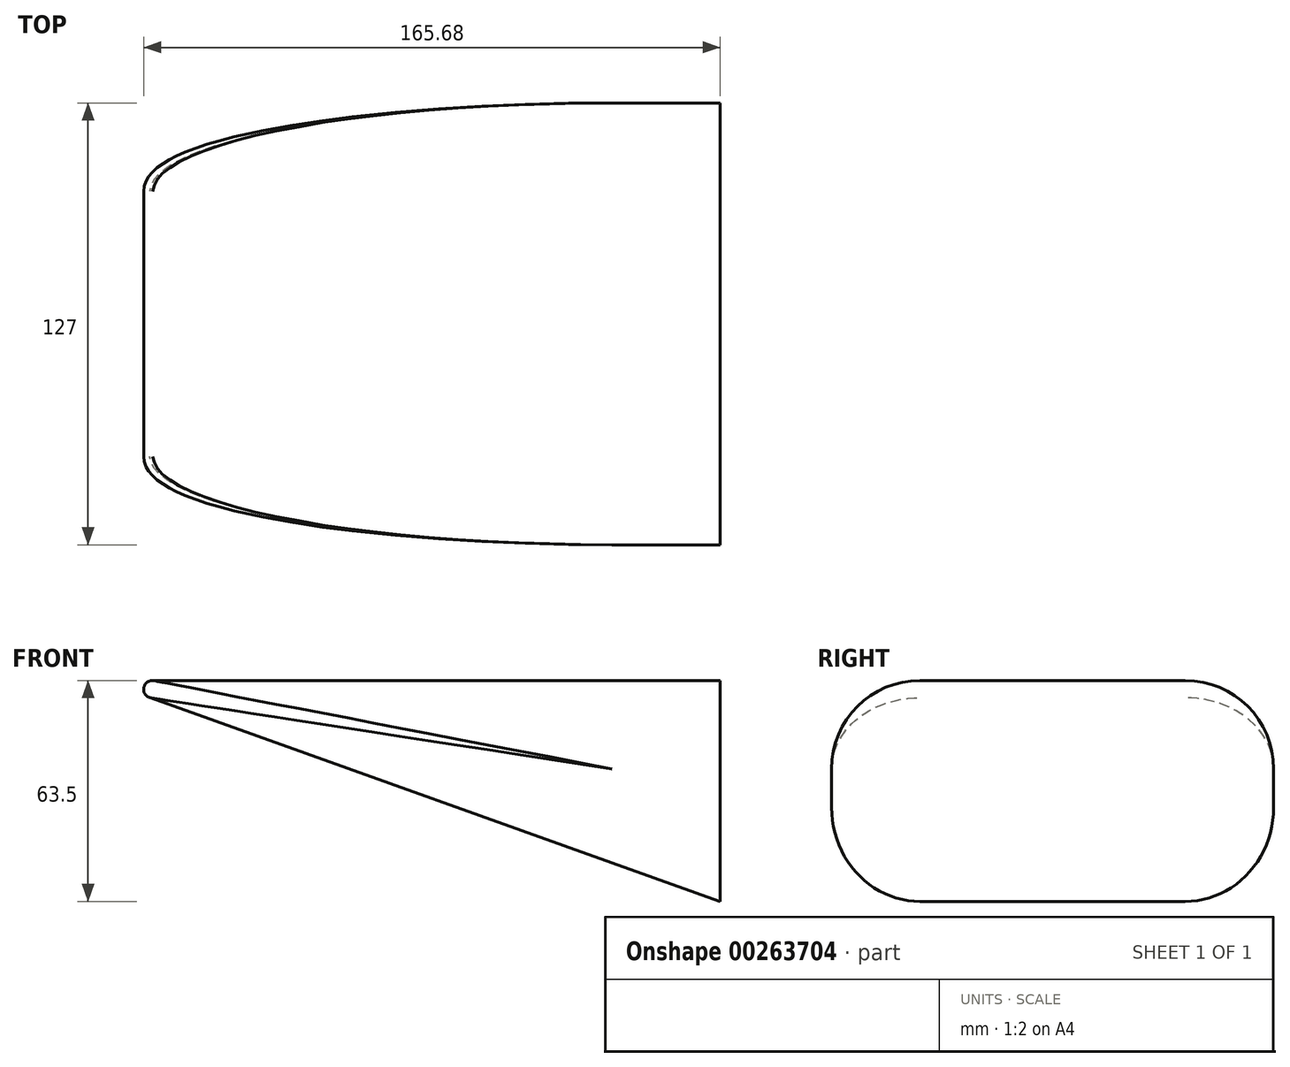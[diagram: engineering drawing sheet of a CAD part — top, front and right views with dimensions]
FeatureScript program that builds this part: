
annotation { "Feature Type Name" : "Feature", "Feature Type Description" : "" }
export const myFeature = defineFeature(function(context is Context, id is Id, definition is map)
    precondition{}
    {
        {
            var Q0;
            Q0=qCreatedBy(makeId("Front.planeOp"),FACE);
            var sketch = newSketch(context, id + "F0", { "sketchPlane" : qUnion([Q0])});
            skLineSegment(sketch, "E0", {"start": v(-43.3, 17.59) * mm, "end": v(-43.3, -45.91) * mm});
            skLineSegment(sketch, "E1", {"start": v(-43.3, 17.59) * mm, "end": v(-206.44, 17.59) * mm});
            skLineSegment(sketch, "E2", {"start": v(-207.3, 12.65) * mm, "end": v(-43.3, -45.91) * mm});
            skPoint(sketch, "E3.visualSharp", {"position": v(-221.1, 17.59) * mm});
            skArc(sketch, "E3.filletArc", {"start": v(-206.44, 17.59) * mm, "mid": v(-208.94, 15.48) * mm, "end": v(-207.3, 12.65) * mm});
            skSolve(sketch);
        }
        {
            var Q0;
            Q0=makeQuery(id+"F0.imprint","IMPRINT",FACE,{"disambiguationData":[TD([[makeQuery(id+"F0.imprint","IMPRINT",EDGE,{"derivedFrom":sQuery(id+"F0.wireOp",EDGE,"E0")}),-1.0]])]});
            extrude(context, id + "F1", {"entities" : qUnion([Q0]), "endBound" : BoundingType.SYMMETRIC, "depth" : 127 * mm});
        }
        {
            var Q0;
            Q0=makeQuery(id+"F1.opExtrude","CAP_EDGE",EDGE,{"disambiguationData":[OSD([sQuery(id+"F0.wireOp",EDGE,"E2")])],"isStart":false});
            var Q1;
            Q1=makeQuery(id+"F1.opExtrude","CAP_EDGE",EDGE,{"disambiguationData":[OSD([sQuery(id+"F0.wireOp",EDGE,"E2")])],"isStart":true});
            fillet(context, id + "F2", {"entities" : qUnion([Q0, Q1]), "radius" : 25.4 * mm, "tangentPropagation" : true, "allowEdgeOverflow" : false});
        }
    });
